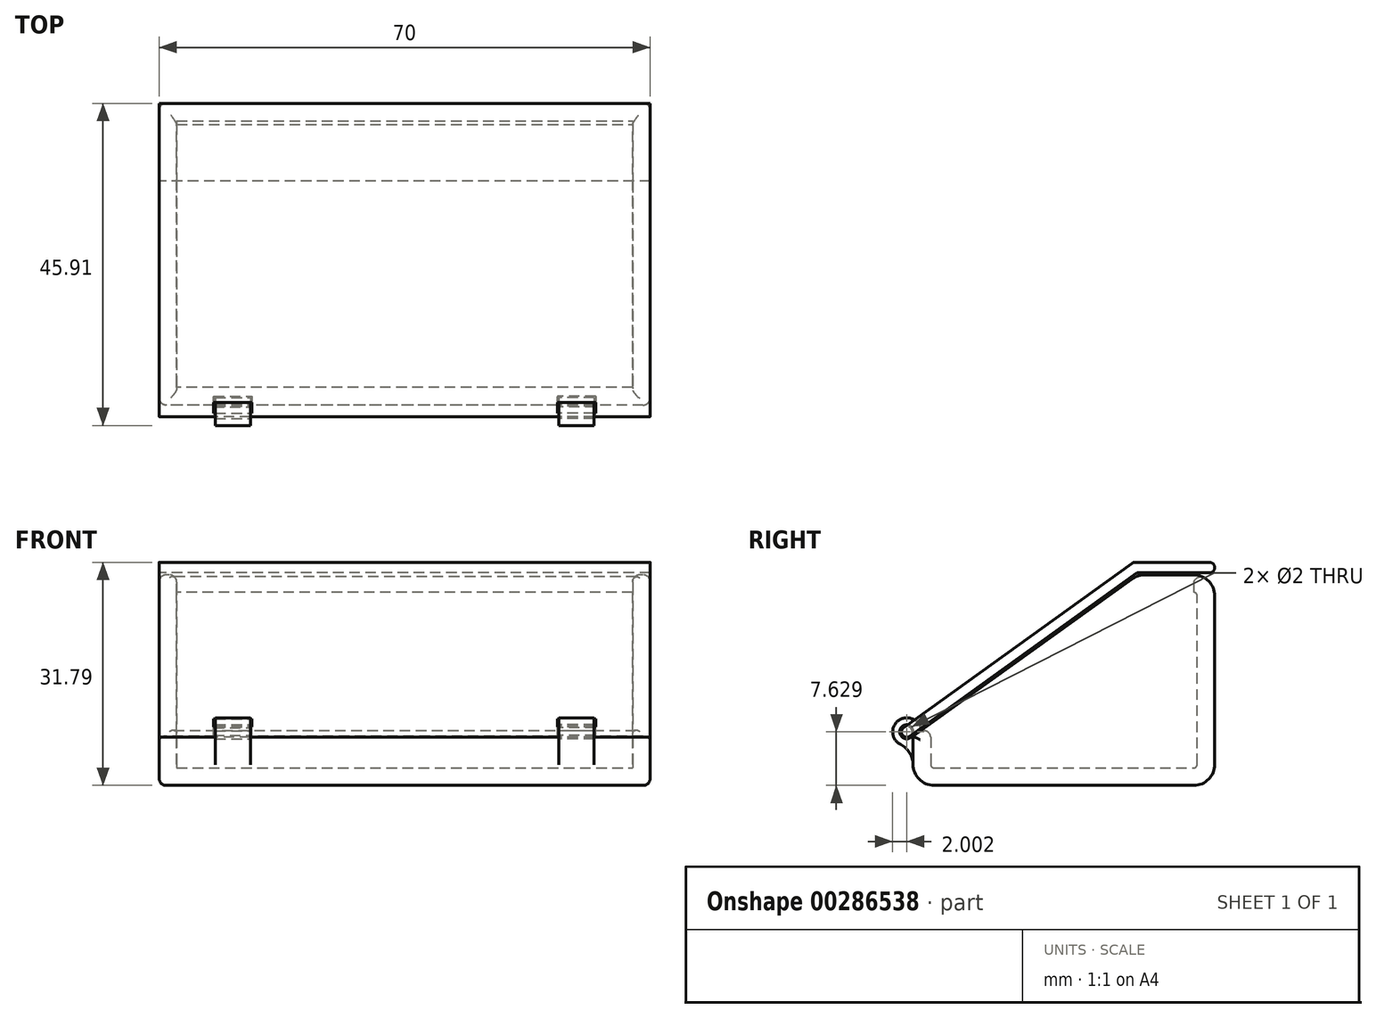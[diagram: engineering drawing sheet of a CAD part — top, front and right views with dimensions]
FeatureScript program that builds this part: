
annotation { "Feature Type Name" : "Feature", "Feature Type Description" : "" }
export const myFeature = defineFeature(function(context is Context, id is Id, definition is map)
    precondition{}
    {
        {
            var Q0;
            Q0=qCreatedBy(makeId("Right.planeOp"),FACE);
            var sketch = newSketch(context, id + "F0", { "sketchPlane" : qUnion([Q0])});
            skLineSegment(sketch, "E0", {"start": v(3, 0) * mm, "end": v(40, 0) * mm});
            skLineSegment(sketch, "E1", {"start": v(43, 3) * mm, "end": v(43, 27) * mm});
            skLineSegment(sketch, "E2", {"start": v(40, 30) * mm, "end": v(32.97, 30) * mm});
            skLineSegment(sketch, "E3", {"start": v(31.22, 29.44) * mm, "end": v(0, 7) * mm});
            skLineSegment(sketch, "E4", {"start": v(0, 7) * mm, "end": v(0, 3) * mm});
            skPoint(sketch, "E5.visualSharp", {"position": v(32, 30) * mm});
            skArc(sketch, "E5.filletArc", {"start": v(32.97, 30) * mm, "mid": v(32.05, 29.86) * mm, "end": v(31.22, 29.44) * mm});
            skPoint(sketch, "E6.visualSharp", {"position": v(43, 30) * mm});
            skArc(sketch, "E6.filletArc", {"start": v(43, 27) * mm, "mid": v(42.12, 29.12) * mm, "end": v(40, 30) * mm});
            skPoint(sketch, "E7.visualSharp", {"position": v(43, 0) * mm});
            skArc(sketch, "E7.filletArc", {"start": v(40, 0) * mm, "mid": v(42.12, 0.88) * mm, "end": v(43, 3) * mm});
            skPoint(sketch, "E8.visualSharp", {"position": v(0, 0) * mm});
            skArc(sketch, "E8.filletArc", {"start": v(0, 3) * mm, "mid": v(0.88, 0.88) * mm, "end": v(3, 0) * mm});
            skSolve(sketch);
        }
        {
            var Q0;
            Q0 = qSketchRegion(id + "F0", true);
            extrude(context, id + "F1", {"entities" : qUnion([Q0]), "depth" : 70 * mm, "symmetric" : true});
        }
        {
            var Q0;
            Q0=makeQuery(id+"F1.opExtrude","SWEPT_FACE",FACE,{"disambiguationData":[OSD([sQuery(id+"F0.wireOp",EDGE,"E3")])]});
            var Q1;
            Q1=makeQuery(id+"F1.opExtrude","SWEPT_FACE",FACE,{"disambiguationData":[OSD([sQuery(id+"F0.wireOp",EDGE,"E2")])]});
            var Q2;
            Q2=makeQuery(id+"F1.opExtrude","SWEPT_FACE",FACE,{"disambiguationData":[OSD([sQuery(id+"F0.wireOp",EDGE,"E5.filletArc")])]});
            shell(context, id + "F2", {"entities" : qUnion([Q0, Q1, Q2]), "thickness" : 2.5 * mm});
        }
        {
            var Q0;
            Q0=makeQuery(id+"F1.opExtrude","CAP_EDGE",EDGE,{"disambiguationData":[OSD([sQuery(id+"F0.wireOp",EDGE,"E4")])],"isStart":false});
            var Q1;
            Q1=makeQuery(id+"F1.opExtrude","CAP_EDGE",EDGE,{"disambiguationData":[OSD([sQuery(id+"F0.wireOp",EDGE,"E4")])],"isStart":true});
            var Q2;
            {var subQ0=sQuery(id+"F0.wireOp",EDGE,"E3");Q2=makeQuery(id+"F2.opShell","OFFSET_EDGE",EDGE,{"disambiguationData":[OSD([subQ0]),TDD([makeQuery(id+"F1.opExtrude","CAP_EDGE",EDGE,{"disambiguationData":[OSD([subQ0])],"isStart":true})])]});}
            var Q3;
            Q3=makeQuery(id+"F2.opShell","OFFSET_EDGE",EDGE,{"disambiguationData":[OSD([sQuery(id+"F0.wireOp",EDGE,"E3"),sQuery(id+"F0.wireOp",EDGE,"E4")])]});
            var Q4;
            {var subQ0=sQuery(id+"F0.wireOp",EDGE,"E3");Q4=makeQuery(id+"F2.opShell","OFFSET_EDGE",EDGE,{"disambiguationData":[OSD([subQ0]),TDD([makeQuery(id+"F1.opExtrude","CAP_EDGE",EDGE,{"disambiguationData":[OSD([subQ0])],"isStart":false})])]});}
            var Q5;
            Q5=makeQuery(id+"F2.opShell","OFFSET_EDGE",EDGE,{"disambiguationData":[OSD([sQuery(id+"F0.wireOp",EDGE,"E2"),sQuery(id+"F0.wireOp",EDGE,"E6.filletArc")]),OD(1.0)]});
            fillet(context, id + "F3", {"entities" : qUnion([Q0, Q1, Q2, Q3, Q4, Q5]), "radius" : 1 * mm, "tangentPropagation" : true, "allowEdgeOverflow" : false});
        }
        {
            var Q0;
            Q0=qCreatedBy(makeId("Right.planeOp"),FACE);
            var sketch = newSketch(context, id + "F4", { "sketchPlane" : qUnion([Q0])});
            skCircle(sketch, "E9", {"center": v(-0.9, 7.63) * mm, "radius": 1 * mm});
            skCircle(sketch, "E10", {"center": v(-0.9, 7.63) * mm, "radius": 2 * mm});
            skSolve(sketch);
        }
        {
            var Q0;
            Q0 = qSketchRegion(id + "F4", true);
            extrude(context, id + "F5", {"entities" : qUnion([Q0]), "operationType" : NewBodyOperationType.ADD, "depth" : 27 * mm, "hasSecondDirection" : true, "secondDirectionOppositeDirection" : false, "secondDirectionDepth" : 22 * mm});
        }
        {
            var Q0;
            Q0 = qSketchRegion(id + "F4", true);
            extrude(context, id + "F6", {"entities" : qUnion([Q0]), "operationType" : NewBodyOperationType.ADD, "oppositeDirection" : true, "depth" : 27 * mm, "hasSecondDirection" : true, "secondDirectionOppositeDirection" : true, "secondDirectionDepth" : 22 * mm});
        }
        {
            var Q0;
            Q0=makeQuery(id+"F6.boolean.opBoolean","INTERSECT",EDGE,{"derivedFrom":[makeQuery(id+"F1.opExtrude","SWEPT_FACE",FACE,{"disambiguationData":[OSD([sQuery(id+"F0.wireOp",EDGE,"E4")])]}),makeQuery(id+"F6.opExtrude","SWEPT_FACE",FACE,{"disambiguationData":[OSD([sQuery(id+"F4.wireOp",EDGE,"E10")])]})]});
            var Q1;
            Q1=makeQuery(id+"F5.boolean.opBoolean","INTERSECT",EDGE,{"derivedFrom":[makeQuery(id+"F1.opExtrude","SWEPT_FACE",FACE,{"disambiguationData":[OSD([sQuery(id+"F0.wireOp",EDGE,"E4")])]}),makeQuery(id+"F5.opExtrude","SWEPT_FACE",FACE,{"disambiguationData":[OSD([sQuery(id+"F4.wireOp",EDGE,"E10")])]})]});
            fillet(context, id + "F7", {"entities" : qUnion([Q0, Q1]), "radius" : 3.3 * mm, "tangentPropagation" : true, "allowEdgeOverflow" : false});
        }
        {
            var Q0;
            Q0=makeQuery(id+"F5.opExtrude","CAP_FACE",FACE,{"disambiguationData":[OSD([sQuery(id+"F4.wireOp",EDGE,"E9"),sQuery(id+"F4.wireOp",EDGE,"E10")])],"isStart":false});
            var sketch = newSketch(context, id + "F8", { "sketchPlane" : qUnion([Q0])});
            skLineSegment(sketch, "E11.0", {"start": v(0, 7) * mm, "end": v(31.22, 29.44) * mm, "construction": true});
            skLineSegment(sketch, "E12.0", {"start": v(32.97, 30) * mm, "end": v(40, 30) * mm, "construction": true});
            skLineSegment(sketch, "E13", {"start": v(-0.9, 7.63) * mm, "end": v(31.66, 31.04) * mm});
            skLineSegment(sketch, "E14.0", {"start": v(31.66, 31.04) * mm, "end": v(42.25, 31.04) * mm});
            skArc(sketch, "E15.0.startCap", {"start": v(-0.47, 7.02) * mm, "mid": v(-1.52, 7.2) * mm, "end": v(-1.35, 8.24) * mm});
            skArc(sketch, "E15.0.endCap", {"start": v(31.23, 31.65) * mm, "mid": v(32.27, 31.48) * mm, "end": v(32.1, 30.43) * mm});
            skLineSegment(sketch, "E15.0.left", {"start": v(-1.35, 8.24) * mm, "end": v(31.23, 31.65) * mm});
            skLineSegment(sketch, "E15.0.right", {"start": v(-0.47, 7.02) * mm, "end": v(32.1, 30.43) * mm});
            skArc(sketch, "E15.1.startCap", {"start": v(31.66, 30.3) * mm, "mid": v(30.91, 31.04) * mm, "end": v(31.66, 31.8) * mm});
            skArc(sketch, "E15.1.endCap", {"start": v(42.25, 31.8) * mm, "mid": v(43, 31.04) * mm, "end": v(42.25, 30.3) * mm});
            skLineSegment(sketch, "E15.1.left", {"start": v(31.66, 31.8) * mm, "end": v(42.25, 31.8) * mm});
            skLineSegment(sketch, "E15.1.right", {"start": v(31.66, 30.3) * mm, "end": v(42.25, 30.3) * mm});
            skLineSegment(sketch, "E16.0", {"start": v(43, 27) * mm, "end": v(43, 3) * mm, "construction": true});
            skLineSegment(sketch, "E17", {"start": v(43, 27) * mm, "end": v(43, 34.78) * mm, "construction": true});
            skSolve(sketch);
        }
        {
            var Q0;
            Q0 = qSketchRegion(id + "F8", true);
            var Q1;
            Q1=makeQuery(id+"F1.opExtrude","CAP_FACE",FACE,{"disambiguationData":[OSD([sQuery(id+"F0.wireOp",EDGE,"E0"),sQuery(id+"F0.wireOp",EDGE,"E1"),sQuery(id+"F0.wireOp",EDGE,"E2"),sQuery(id+"F0.wireOp",EDGE,"E3"),sQuery(id+"F0.wireOp",EDGE,"E4"),sQuery(id+"F0.wireOp",EDGE,"E5.filletArc"),sQuery(id+"F0.wireOp",EDGE,"E6.filletArc"),sQuery(id+"F0.wireOp",EDGE,"E7.filletArc"),sQuery(id+"F0.wireOp",EDGE,"E8.filletArc")])],"isStart":false});
            var Q2;
            Q2=makeQuery(id+"F1.opExtrude","CAP_FACE",FACE,{"disambiguationData":[OSD([sQuery(id+"F0.wireOp",EDGE,"E0"),sQuery(id+"F0.wireOp",EDGE,"E1"),sQuery(id+"F0.wireOp",EDGE,"E2"),sQuery(id+"F0.wireOp",EDGE,"E3"),sQuery(id+"F0.wireOp",EDGE,"E4"),sQuery(id+"F0.wireOp",EDGE,"E5.filletArc"),sQuery(id+"F0.wireOp",EDGE,"E6.filletArc"),sQuery(id+"F0.wireOp",EDGE,"E7.filletArc"),sQuery(id+"F0.wireOp",EDGE,"E8.filletArc")])],"isStart":true});
            extrude(context, id + "F9", {"entities" : qUnion([Q0]), "endBound" : BoundingType.UP_TO_SURFACE, "endBoundEntityFace" : qUnion([Q1]), "depth" : 25 * mm, "hasSecondDirection" : true, "secondDirectionBound" : BoundingType.UP_TO_SURFACE, "secondDirectionOppositeDirection" : true, "secondDirectionBoundEntityFace" : qUnion([Q2]), "secondDirectionDepth" : 25 * mm});
        }
        {
            var Q0;
            Q0=makeQuery(id+"F1.opExtrude","SWEPT_BODY",BODY,{"disambiguationData":[OSD([sQuery(id+"F0.wireOp",EDGE,"E0"),sQuery(id+"F0.wireOp",EDGE,"E1"),sQuery(id+"F0.wireOp",EDGE,"E2"),sQuery(id+"F0.wireOp",EDGE,"E3"),sQuery(id+"F0.wireOp",EDGE,"E4"),sQuery(id+"F0.wireOp",EDGE,"E5.filletArc"),sQuery(id+"F0.wireOp",EDGE,"E6.filletArc"),sQuery(id+"F0.wireOp",EDGE,"E7.filletArc"),sQuery(id+"F0.wireOp",EDGE,"E8.filletArc")])]});
            var Q1;
            Q1=makeQuery(id+"F9.opExtrude","SWEPT_BODY",BODY,{"disambiguationData":[OSD([sQuery(id+"F8.wireOp",EDGE,"E15.0.startCap"),sQuery(id+"F8.wireOp",EDGE,"E15.0.left"),sQuery(id+"F8.wireOp",EDGE,"E15.0.right"),sQuery(id+"F8.wireOp",EDGE,"E15.1.startCap"),sQuery(id+"F8.wireOp",EDGE,"E15.1.endCap"),sQuery(id+"F8.wireOp",EDGE,"E15.1.left"),sQuery(id+"F8.wireOp",EDGE,"E15.1.right")])]});
            var Q2;
            Q2=makeQuery(id+"F5.opExtrude","CAP_FACE",FACE,{"disambiguationData":[OSD([sQuery(id+"F4.wireOp",EDGE,"E9"),sQuery(id+"F4.wireOp",EDGE,"E10")])],"isStart":false});
            var Q3;
            Q3=makeQuery(id+"F5.opExtrude","SWEPT_FACE",FACE,{"disambiguationData":[OSD([sQuery(id+"F4.wireOp",EDGE,"E10")])]});
            var Q4;
            Q4=makeQuery(id+"F5.opExtrude","CAP_FACE",FACE,{"disambiguationData":[OSD([sQuery(id+"F4.wireOp",EDGE,"E9"),sQuery(id+"F4.wireOp",EDGE,"E10")])],"isStart":true});
            var Q5;
            Q5=makeQuery(id+"F5.opExtrude","SWEPT_FACE",FACE,{"disambiguationData":[OSD([sQuery(id+"F4.wireOp",EDGE,"E9")])]});
            var Q6;
            Q6=makeQuery(id+"F6.opExtrude","SWEPT_FACE",FACE,{"disambiguationData":[OSD([sQuery(id+"F4.wireOp",EDGE,"E10")])]});
            var Q7;
            Q7=makeQuery(id+"F6.opExtrude","SWEPT_FACE",FACE,{"disambiguationData":[OSD([sQuery(id+"F4.wireOp",EDGE,"E9")])]});
            var Q8;
            Q8=makeQuery(id+"F6.opExtrude","CAP_FACE",FACE,{"disambiguationData":[OSD([sQuery(id+"F4.wireOp",EDGE,"E9"),sQuery(id+"F4.wireOp",EDGE,"E10")])],"isStart":true});
            var Q9;
            Q9=makeQuery(id+"F6.opExtrude","CAP_FACE",FACE,{"disambiguationData":[OSD([sQuery(id+"F4.wireOp",EDGE,"E9"),sQuery(id+"F4.wireOp",EDGE,"E10")])],"isStart":false});
            booleanBodies(context, id + "F10", {"operationType" : BooleanOperationType.SUBTRACTION, "tools" : qUnion([Q0]), "targets" : qUnion([Q1]), "offset" : true, "entitiesToOffset" : qUnion([Q2, Q3, Q4, Q5, Q6, Q7, Q8, Q9]), "offsetDistance" : .22 * mm, "keepTools" : true});
        }
    });
